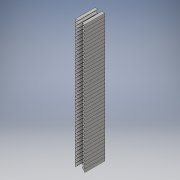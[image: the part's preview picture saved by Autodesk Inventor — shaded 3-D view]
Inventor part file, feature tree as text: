
AUTODESK INVENTOR PART (.ipt)
format: ipt  version: 2016 (Build 200138000, 138)  size: 260,096 bytes
history: native  units: in
note: dims shown in document units (in); Inventor stores cm internally (conversion verified against a paired STEP export)
features: extrude x1, pattern_linear x1, sketch x1
ambient origin geometry x8: Origin, YZ Plane, XZ Plane, XY Plane, X Axis, Y Axis, Z Axis, Center Point
bodies: Solid1 (feature_tree)
feature tree (3):
  extrude  "Extrusion1"  Depth=0.025in
  pattern_linear  "Rectangular Pattern1"  Spacing1=0.0375in  [1 undecoded]
  sketch  "Sketch1"  dims[d0=0.0247in d1=0.025in d2=0.0375in d3=0.0223in d4=0.154in d5=0.0in d6=15.748in d8=0.025in]
note: 1 required parameter value undecoded (feature->parameter linkage not recoverable at this tier; creation-order binding heuristic only, values carry confidence <= 0.55)
